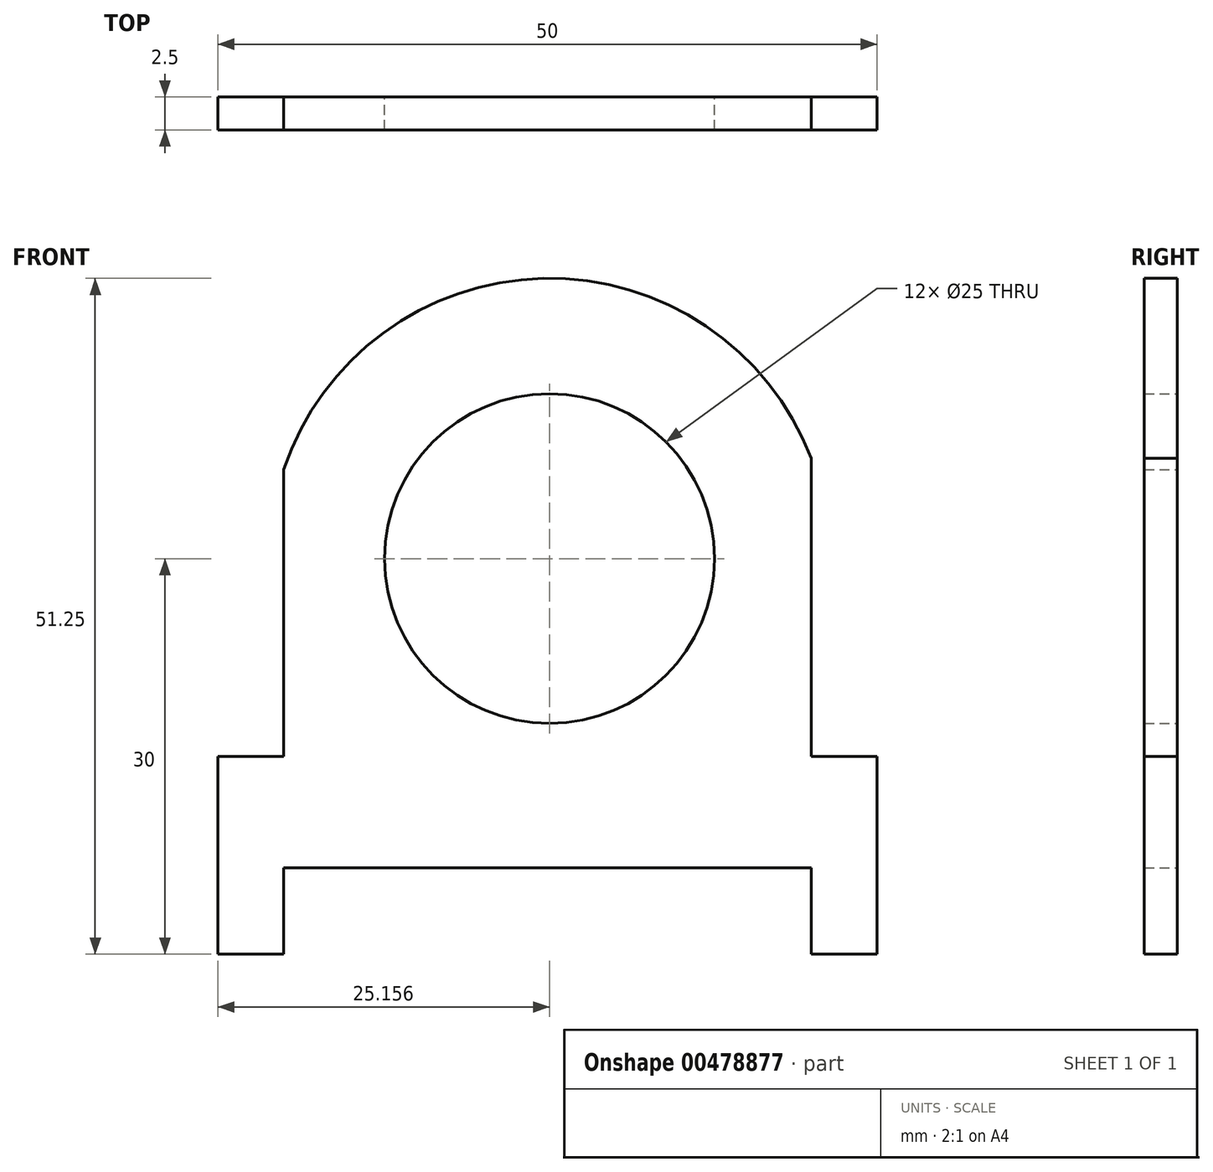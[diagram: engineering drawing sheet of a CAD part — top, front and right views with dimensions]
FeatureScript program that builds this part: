
annotation { "Feature Type Name" : "Feature", "Feature Type Description" : "" }
export const myFeature = defineFeature(function(context is Context, id is Id, definition is map)
    precondition{}
    {
        {
            var Q0;
            Q0=qCreatedBy(makeId("Front.planeOp"),FACE);
            var sketch = newSketch(context, id + "F0", { "sketchPlane" : qUnion([Q0])});
            skLineSegment(sketch, "E0", {"start": v(0, 0) * mm, "end": v(-5, 0) * mm});
            skLineSegment(sketch, "E1", {"start": v(-5, 0) * mm, "end": v(-5, 6.54) * mm});
            skLineSegment(sketch, "E2", {"start": v(-5, 6.54) * mm, "end": v(-45, 6.54) * mm});
            skLineSegment(sketch, "E3", {"start": v(-45, 6.54) * mm, "end": v(-45, 0) * mm});
            skLineSegment(sketch, "E4", {"start": v(-45, 0) * mm, "end": v(-50, 0) * mm});
            skLineSegment(sketch, "E5", {"start": v(-50, 0) * mm, "end": v(-50, 15) * mm});
            skLineSegment(sketch, "E6", {"start": v(-50, 15) * mm, "end": v(-45, 15) * mm});
            skLineSegment(sketch, "E7", {"start": v(-45, 15) * mm, "end": v(-45, 36.73) * mm});
            skLineSegment(sketch, "E8", {"start": v(-5, 37.6) * mm, "end": v(-5, 15) * mm});
            skLineSegment(sketch, "E9", {"start": v(-5, 15) * mm, "end": v(0, 15) * mm});
            skLineSegment(sketch, "E10", {"start": v(0, 15) * mm, "end": v(0, 0) * mm});
            skArc(sketch, "E11", {"start": v(-5, 37.6) * mm, "mid": v(-25.3, 51.24) * mm, "end": v(-45, 36.73) * mm});
            skCircle(sketch, "E12", {"center": v(-24.84, 30) * mm, "radius": 12.5 * mm});
            skSolve(sketch);
        }
        {
            var Q0;
            Q0=makeQuery(id+"F0.imprint","IMPRINT",FACE,{"disambiguationData":[TD([[makeQuery(id+"F0.imprint","IMPRINT",EDGE,{"derivedFrom":sQuery(id+"F0.wireOp",EDGE,"E0")}),-1.0]])]});
            extrude(context, id + "F1", {"entities" : qUnion([Q0]), "depth" : 2.5 * mm});
        }
    });
